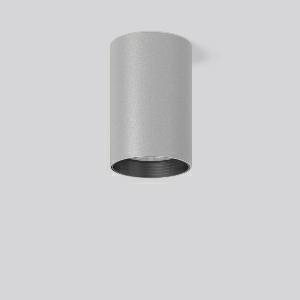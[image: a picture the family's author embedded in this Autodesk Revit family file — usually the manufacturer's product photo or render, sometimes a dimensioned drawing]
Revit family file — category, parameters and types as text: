
# Revit family: heledon_maxi_a_931221_004_e952
name_source: partatom
category: Lighting Fixtures
units: mm (PartAtom-declared; Revit-internal decimal feet)

## family parameters
Cut with Voids When Loaded = No
Host = Face
Light Source = No
Part Type = Normal
Room Calculation Point = No
Round Connector Dimension = Use Diameter
Shared = No

## types (1)
- HELEDON maxi A (1 x LED Modul 930, 2750 lm, 3000)
    Apparent Load = 25 VA
    Approval mark = CE
    CIE Flux Codes = 96 100 100 100 100
    Color Rendering = 90
    Color Temperature = 3000
    Default Elevation = 1800 mm
    Description = Series: HELEDON maxi
Cylindrical surface-mounted downlight. Housing: die-cast aluminium, powder-coated. Internal ceiling frame polycarbonate with bayonet mounting. Black plastic ring and recessed LED to prevent glare from the side. Optical assembly with lens made of plastic (polycarbonate) for the best homogeneous light distribution - can be changed without tools. Best colour rendering index Ra>90. Suitable for Ceiling mounting. Easy installation with a separate ceiling frame with bayonet mounting and plug connection. Driver integrated. Connected via plug-in connector. High quality converter without flickering and stroboscopic effect. The following accessories can be mounted without use of tools: interchangeable lenses, decorative glasses, honeycomb louvre, clear and frosted diffusers, white interchangeable plastic ring. 
Colour: silver
Diameter: 123 mm
Height: 183 mm
Lamp: LED
Socket: without socket
Colour temperature: 3000K
Colour rendering index (CRI): 92
System power: 25 W
Rated luminous flux: 2750 lm
Luminous efficiency: 110 lm/W
Control gear: Regulated power supply
Protection class: I
Type of protection: IP 20
    Height = 183 mm
    Lamp = 1 x LED Modul 930
    Lamp Light Flux = 2750 lm
    Lamp count = 1
    Length = 123 mm
    Lifetime = 50000 h
    Luminous efficacy = 110 lm/W
    Manufacturer = RZB
    ModVariant = No
    Model = 931221.004
    Mounting Place = Ceiling
    Mounting Type = Surface mounted
    Number of Poles = 1
    OnlyDefault = Yes
    Power Factor = 1
    Product Name = HELEDON maxi A
    Product group = Surface mounted downlights
    ProductGroupID = 302
    Protection Class = Protection class I
    Protection Degree = IP 20
    RLX_Detail_Level = 1
    RLX_Emergency_Light_Flux = 0 lm
    RLX_Emergency_Type = 0
    RLX_Emergency_Type_DB = No
    RlxData = <blob elided: 100249 chars, md5=8d28d89d>
    Socket = socket
    Standby Power = 0 W
    System Light Flux = 2750 lm
    System Power = 25 W
    Type Comments = Product without accessories
    Type Image = 931193.004.jpg
    URL = http://relux.com
    VarID = ---
    Voltage = 230 V
    Voltage Range = 220-240 V
    Weight = 0.00 kg
    Width = 0 mm  [stored 0 ft]

note: [stored X ft] marks values corroborated as IEEE doubles in the binary element streams (Revit-internal decimal feet)

## geometry (parser evidence)
native form markers: Blend x4, Sweep x10
no freeform markers — native parametric forms only
